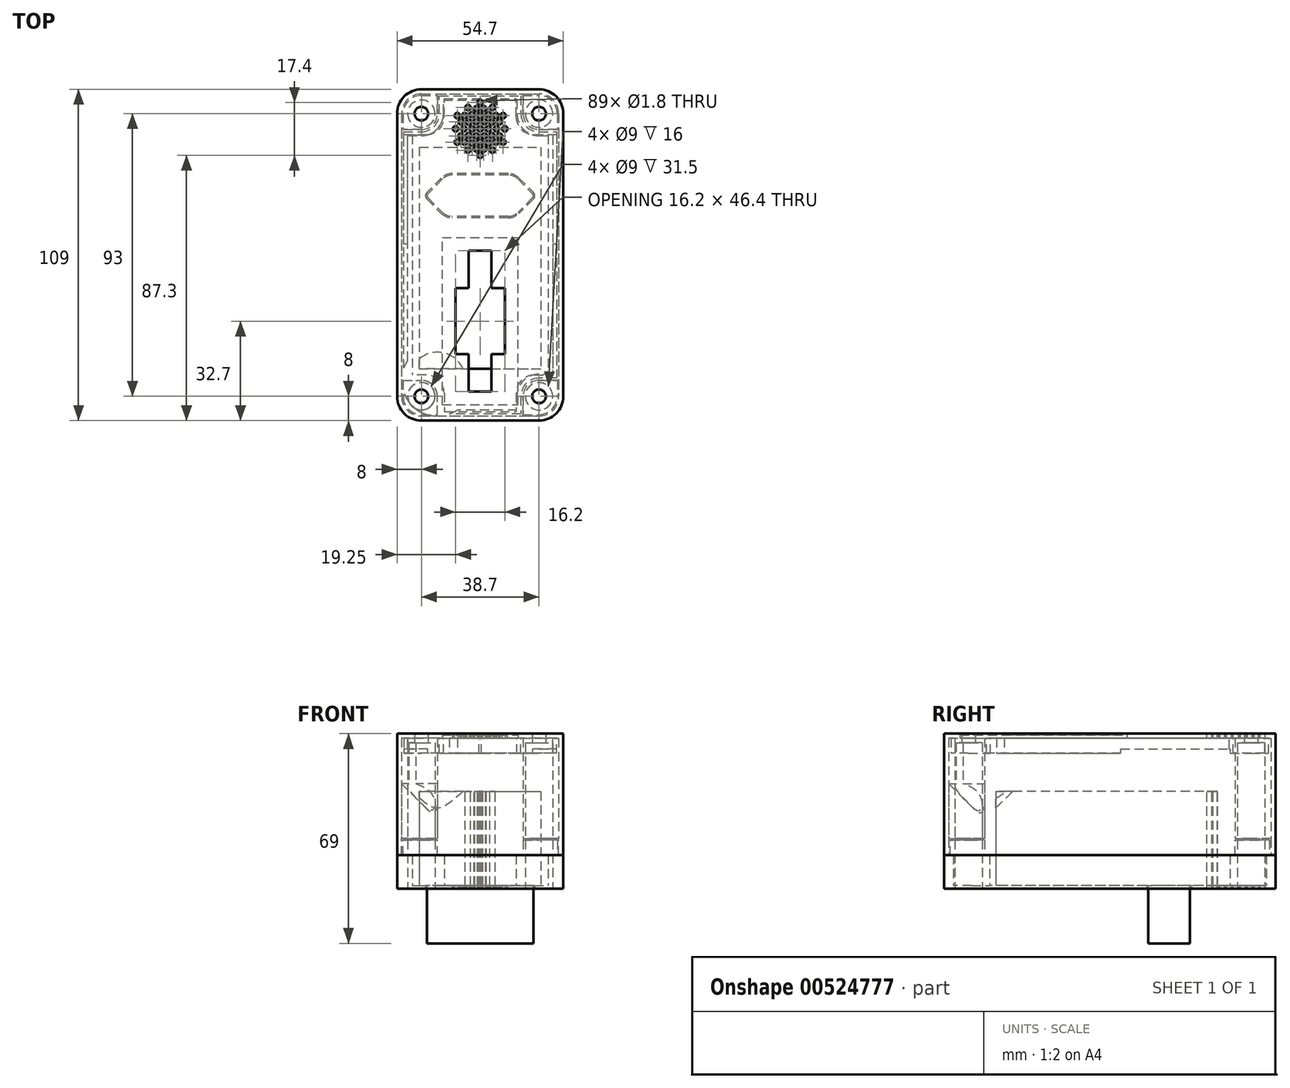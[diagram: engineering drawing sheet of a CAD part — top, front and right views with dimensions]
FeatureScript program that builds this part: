
annotation { "Feature Type Name" : "Feature", "Feature Type Description" : "" }
export const myFeature = defineFeature(function(context is Context, id is Id, definition is map)
    precondition{}
    {
        {
            var Q0;
            Q0=qCreatedBy(makeId("Top.planeOp"),FACE);
            var sketch = newSketch(context, id + "F0", { "sketchPlane" : qUnion([Q0])});
            skLineSegment(sketch, "E0.bottom", {"start": v(9.23, 7.3) * mm, "end": v(-9.23, 7.3) * mm});
            skLineSegment(sketch, "E0.top", {"start": v(9.23, -7.3) * mm, "end": v(-9.23, -7.3) * mm});
            skPoint(sketch, "E0.middle", {"position": v(0, 0) * mm});
            skLineSegment(sketch, "E1", {"start": v(12.76, 5.84) * mm, "end": v(17.54, 1.06) * mm});
            skLineSegment(sketch, "E2", {"start": v(17.54, -1.06) * mm, "end": v(12.76, -5.84) * mm});
            skLineSegment(sketch, "E3.MirrorCS", {"start": v(-12.76, 5.84) * mm, "end": v(-17.54, 1.06) * mm});
            skLineSegment(sketch, "E4.MirrorCS", {"start": v(-17.54, -1.06) * mm, "end": v(-12.76, -5.84) * mm});
            skPoint(sketch, "E5.visualSharp", {"position": v(-11.3, 7.3) * mm});
            skArc(sketch, "E5.filletArc", {"start": v(-9.23, 7.3) * mm, "mid": v(-11.14, 6.92) * mm, "end": v(-12.76, 5.84) * mm});
            skPoint(sketch, "E6.visualSharp", {"position": v(11.3, 7.3) * mm});
            skArc(sketch, "E6.filletArc", {"start": v(12.76, 5.84) * mm, "mid": v(11.14, 6.92) * mm, "end": v(9.23, 7.3) * mm});
            skPoint(sketch, "E7.visualSharp", {"position": v(11.3, -7.3) * mm});
            skArc(sketch, "E7.filletArc", {"start": v(9.23, -7.3) * mm, "mid": v(11.14, -6.92) * mm, "end": v(12.76, -5.84) * mm});
            skPoint(sketch, "E8.visualSharp", {"position": v(-11.3, -7.3) * mm});
            skArc(sketch, "E8.filletArc", {"start": v(-12.76, -5.84) * mm, "mid": v(-11.14, -6.92) * mm, "end": v(-9.23, -7.3) * mm});
            skPoint(sketch, "E9.visualSharp", {"position": v(-18.6, 0) * mm});
            skArc(sketch, "E9.filletArc", {"start": v(-17.54, 1.06) * mm, "mid": v(-17.98, 0) * mm, "end": v(-17.54, -1.06) * mm});
            skPoint(sketch, "E10.visualSharp", {"position": v(18.6, 0) * mm});
            skArc(sketch, "E10.filletArc", {"start": v(17.54, -1.06) * mm, "mid": v(17.98, 0) * mm, "end": v(17.54, 1.06) * mm});
            skLineSegment(sketch, "E11.bottom", {"start": v(-19.35, 35) * mm, "end": v(19.35, 35) * mm});
            skLineSegment(sketch, "E11.top", {"start": v(-19.35, -74) * mm, "end": v(19.35, -74) * mm});
            skLineSegment(sketch, "E11.left", {"start": v(-27.35, 27) * mm, "end": v(-27.35, -66) * mm});
            skLineSegment(sketch, "E11.right", {"start": v(27.35, 27) * mm, "end": v(27.35, -66) * mm});
            skPoint(sketch, "E12.visualSharp", {"position": v(27.35, 35) * mm});
            skArc(sketch, "E12.filletArc", {"start": v(27.35, 27) * mm, "mid": v(25, 32.66) * mm, "end": v(19.35, 35) * mm});
            skPoint(sketch, "E13.visualSharp", {"position": v(-27.35, 35) * mm});
            skArc(sketch, "E13.filletArc", {"start": v(-19.35, 35) * mm, "mid": v(-25, 32.66) * mm, "end": v(-27.35, 27) * mm});
            skPoint(sketch, "E14.visualSharp", {"position": v(-27.35, -74) * mm});
            skArc(sketch, "E14.filletArc", {"start": v(-27.35, -66) * mm, "mid": v(-25, -71.66) * mm, "end": v(-19.35, -74) * mm});
            skPoint(sketch, "E15.visualSharp", {"position": v(27.35, -74) * mm});
            skArc(sketch, "E15.filletArc", {"start": v(19.35, -74) * mm, "mid": v(25, -71.66) * mm, "end": v(27.35, -66) * mm});
            skLineSegment(sketch, "E16.bottom", {"start": v(-25.35, 25) * mm, "end": v(25.35, 25) * mm, "construction": true});
            skLineSegment(sketch, "E16.top", {"start": v(-25.35, -45) * mm, "end": v(25.35, -45) * mm, "construction": true});
            skLineSegment(sketch, "E16.left", {"start": v(-25.35, 25) * mm, "end": v(-25.35, -45) * mm, "construction": true});
            skLineSegment(sketch, "E16.right", {"start": v(25.35, 25) * mm, "end": v(25.35, -45) * mm, "construction": true});
            skSolve(sketch);
        }
        {
            var Q0;
            Q0=makeQuery(id+"F0.imprint","IMPRINT",FACE,{"disambiguationData":[TD([[makeQuery(id+"F0.imprint","IMPRINT",EDGE,{"derivedFrom":sQuery(id+"F0.wireOp",EDGE,"E0.bottom")}),-1.0]])]});
            extrude(context, id + "F1", {"entities" : qUnion([Q0]), "depth" : 1 * mm, "offsetDistance" : 25 * mm});
        }
        {
            var Q0;
            Q0=makeQuery(id+"F1.opExtrude","CAP_FACE",FACE,{"disambiguationData":[OSD([sQuery(id+"F0.wireOp",EDGE,"E0.bottom"),sQuery(id+"F0.wireOp",EDGE,"E0.top"),sQuery(id+"F0.wireOp",EDGE,"E1"),sQuery(id+"F0.wireOp",EDGE,"E2"),sQuery(id+"F0.wireOp",EDGE,"E3.MirrorCS"),sQuery(id+"F0.wireOp",EDGE,"E4.MirrorCS"),sQuery(id+"F0.wireOp",EDGE,"E5.filletArc"),sQuery(id+"F0.wireOp",EDGE,"E6.filletArc"),sQuery(id+"F0.wireOp",EDGE,"E7.filletArc"),sQuery(id+"F0.wireOp",EDGE,"E8.filletArc"),sQuery(id+"F0.wireOp",EDGE,"E9.filletArc"),sQuery(id+"F0.wireOp",EDGE,"E10.filletArc"),sQuery(id+"F0.wireOp",EDGE,"E11.bottom"),sQuery(id+"F0.wireOp",EDGE,"E11.top"),sQuery(id+"F0.wireOp",EDGE,"E11.left"),sQuery(id+"F0.wireOp",EDGE,"E11.right"),sQuery(id+"F0.wireOp",EDGE,"E12.filletArc"),sQuery(id+"F0.wireOp",EDGE,"E13.filletArc"),sQuery(id+"F0.wireOp",EDGE,"E14.filletArc"),sQuery(id+"F0.wireOp",EDGE,"E15.filletArc")])],"isStart":false});
            var sketch = newSketch(context, id + "F2", { "sketchPlane" : qUnion([Q0])});
            skLineSegment(sketch, "E17.bottom", {"start": v(-22.35, 20) * mm, "end": v(-17.85, 20) * mm});
            skLineSegment(sketch, "E17.top", {"start": v(17.85, -59) * mm, "end": v(22.35, -59) * mm});
            skLineSegment(sketch, "E17.left", {"start": v(-22.35, 20) * mm, "end": v(-22.35, -59) * mm});
            skLineSegment(sketch, "E17.right", {"start": v(22.35, 20) * mm, "end": v(22.35, -59) * mm});
            skCircle(sketch, "E18", {"center": v(19.35, 27) * mm, "radius": 4.5 * mm, "construction": true});
            skCircle(sketch, "E19", {"center": v(-19.35, 27) * mm, "radius": 4.5 * mm, "construction": true});
            skCircle(sketch, "E20", {"center": v(-19.35, -66) * mm, "radius": 4.5 * mm, "construction": true});
            skCircle(sketch, "E21", {"center": v(19.35, -66) * mm, "radius": 4.5 * mm, "construction": true});
            skCircle(sketch, "E22", {"center": v(-19.35, 27) * mm, "radius": 1.75 * mm, "construction": true});
            skCircle(sketch, "E23", {"center": v(19.35, 27) * mm, "radius": 1.75 * mm, "construction": true});
            skCircle(sketch, "E24", {"center": v(19.35, -66) * mm, "radius": 1.75 * mm, "construction": true});
            skCircle(sketch, "E25", {"center": v(-19.35, -66) * mm, "radius": 1.75 * mm, "construction": true});
            skLineSegment(sketch, "E26.top", {"start": v(-11.85, -71) * mm, "end": v(11.85, -71) * mm});
            skLineSegment(sketch, "E26.left", {"start": v(-11.85, -65) * mm, "end": v(-11.85, -71) * mm});
            skLineSegment(sketch, "E26.right", {"start": v(11.85, -65) * mm, "end": v(11.85, -71) * mm});
            skPoint(sketch, "E27.newPointA", {"position": v(11.85, -59) * mm});
            skArc(sketch, "E27.filletArc", {"start": v(17.85, -59) * mm, "mid": v(13.6, -60.76) * mm, "end": v(11.85, -65) * mm});
            skLineSegment(sketch, "E28", {"start": v(-17.85, -59) * mm, "end": v(-22.35, -59) * mm});
            skPoint(sketch, "E29.visualSharp", {"position": v(-11.85, -59) * mm});
            skArc(sketch, "E29.filletArc", {"start": v(-11.85, -65) * mm, "mid": v(-13.6, -60.76) * mm, "end": v(-17.85, -59) * mm});
            skLineSegment(sketch, "E30", {"start": v(27.35, -19.5) * mm, "end": v(-27.35, -19.5) * mm, "construction": true});
            skPoint(sketch, "E30.endSnap0", {"position": v(-27.35, -19.5) * mm});
            skArc(sketch, "E31.MirrorCS", {"start": v(-11.85, 26) * mm, "mid": v(-13.6, 21.76) * mm, "end": v(-17.85, 20) * mm});
            skLineSegment(sketch, "E32.MirrorCS", {"start": v(-11.85, 26) * mm, "end": v(-11.85, 32) * mm});
            skLineSegment(sketch, "E33.MirrorCS", {"start": v(-11.85, 32) * mm, "end": v(11.85, 32) * mm});
            skLineSegment(sketch, "E34.MirrorCS", {"start": v(11.85, 26) * mm, "end": v(11.85, 32) * mm});
            skArc(sketch, "E35.MirrorCS", {"start": v(17.85, 20) * mm, "mid": v(13.6, 21.76) * mm, "end": v(11.85, 26) * mm});
            skLineSegment(sketch, "E36.trimOffspring", {"start": v(17.85, 20) * mm, "end": v(22.35, 20) * mm});
            skSolve(sketch);
        }
        {
            var Q0;
            Q0=makeQuery(id+"F2.imprint","IMPRINT",FACE,{"disambiguationData":[TD([[makeQuery(id+"F2.imprint","IMPRINT",EDGE,{"derivedFrom":sQuery(id+"F2.wireOp",EDGE,"E17.bottom")}),1.0]])]});
            extrude(context, id + "F3", {"entities" : qUnion([Q0]), "operationType" : NewBodyOperationType.ADD, "depth" : 15 * mm, "offsetDistance" : 25 * mm});
        }
        {
            var Q0;
            Q0=makeQuery(id+"F1.opExtrude","CAP_FACE",FACE,{"disambiguationData":[OSD([sQuery(id+"F0.wireOp",EDGE,"E0.bottom"),sQuery(id+"F0.wireOp",EDGE,"E0.top"),sQuery(id+"F0.wireOp",EDGE,"E1"),sQuery(id+"F0.wireOp",EDGE,"E2"),sQuery(id+"F0.wireOp",EDGE,"E3.MirrorCS"),sQuery(id+"F0.wireOp",EDGE,"E4.MirrorCS"),sQuery(id+"F0.wireOp",EDGE,"E5.filletArc"),sQuery(id+"F0.wireOp",EDGE,"E6.filletArc"),sQuery(id+"F0.wireOp",EDGE,"E7.filletArc"),sQuery(id+"F0.wireOp",EDGE,"E8.filletArc"),sQuery(id+"F0.wireOp",EDGE,"E9.filletArc"),sQuery(id+"F0.wireOp",EDGE,"E10.filletArc"),sQuery(id+"F0.wireOp",EDGE,"E11.bottom"),sQuery(id+"F0.wireOp",EDGE,"E11.top"),sQuery(id+"F0.wireOp",EDGE,"E11.left"),sQuery(id+"F0.wireOp",EDGE,"E11.right"),sQuery(id+"F0.wireOp",EDGE,"E12.filletArc"),sQuery(id+"F0.wireOp",EDGE,"E13.filletArc"),sQuery(id+"F0.wireOp",EDGE,"E14.filletArc"),sQuery(id+"F0.wireOp",EDGE,"E15.filletArc")])],"isStart":true});
            var sketch = newSketch(context, id + "F4", { "sketchPlane" : qUnion([Q0])});
            skCircle(sketch, "E37.0", {"center": v(-19.35, 66) * mm, "radius": 1.75 * mm});
            skCircle(sketch, "E38.0", {"center": v(-19.35, 66) * mm, "radius": 4.5 * mm});
            skCircle(sketch, "E39.0", {"center": v(19.35, 66) * mm, "radius": 1.75 * mm});
            skCircle(sketch, "E40.0", {"center": v(19.35, 66) * mm, "radius": 4.5 * mm});
            skCircle(sketch, "E41.0", {"center": v(19.35, -27) * mm, "radius": 1.75 * mm});
            skCircle(sketch, "E42.0", {"center": v(19.35, -27) * mm, "radius": 4.5 * mm});
            skCircle(sketch, "E43.0", {"center": v(-19.35, -27) * mm, "radius": 1.75 * mm});
            skCircle(sketch, "E44.0", {"center": v(-19.35, -27) * mm, "radius": 4.5 * mm});
            skSolve(sketch);
        }
        {
            var Q0;
            Q0=makeQuery(id+"F4.imprint","IMPRINT",FACE,{"disambiguationData":[TD([[makeQuery(id+"F4.imprint","IMPRINT",EDGE,{"derivedFrom":sQuery(id+"F4.wireOp",EDGE,"E37.0")}),1.0]])]});
            var Q1;
            Q1=makeQuery(id+"F4.imprint","IMPRINT",FACE,{"disambiguationData":[TD([[makeQuery(id+"F4.imprint","IMPRINT",EDGE,{"derivedFrom":sQuery(id+"F4.wireOp",EDGE,"E39.0")}),1.0]])]});
            var Q2;
            Q2=makeQuery(id+"F4.imprint","IMPRINT",FACE,{"disambiguationData":[TD([[makeQuery(id+"F4.imprint","IMPRINT",EDGE,{"derivedFrom":sQuery(id+"F4.wireOp",EDGE,"E43.0")}),1.0]])]});
            var Q3;
            Q3=makeQuery(id+"F4.imprint","IMPRINT",FACE,{"disambiguationData":[TD([[makeQuery(id+"F4.imprint","IMPRINT",EDGE,{"derivedFrom":sQuery(id+"F4.wireOp",EDGE,"E41.0")}),1.0]])]});
            extrude(context, id + "F5", {"entities" : qUnion([Q0, Q1, Q2, Q3]), "operationType" : NewBodyOperationType.REMOVE, "oppositeDirection" : true, "depth" : 5.5 * mm, "offsetDistance" : 25 * mm});
        }
        {
            var Q0;
            Q0=makeQuery(id+"F3.opExtrude","CAP_FACE",FACE,{"disambiguationData":[OSD([sQuery(id+"F0.wireOp",EDGE,"E11.bottom"),sQuery(id+"F0.wireOp",EDGE,"E11.top"),sQuery(id+"F0.wireOp",EDGE,"E11.left"),sQuery(id+"F0.wireOp",EDGE,"E11.right"),sQuery(id+"F0.wireOp",EDGE,"E12.filletArc"),sQuery(id+"F0.wireOp",EDGE,"E13.filletArc"),sQuery(id+"F0.wireOp",EDGE,"E14.filletArc"),sQuery(id+"F0.wireOp",EDGE,"E15.filletArc"),sQuery(id+"F2.wireOp",EDGE,"E17.bottom"),sQuery(id+"F2.wireOp",EDGE,"E17.top"),sQuery(id+"F2.wireOp",EDGE,"E17.left"),sQuery(id+"F2.wireOp",EDGE,"E17.right"),sQuery(id+"F2.wireOp",EDGE,"E26.top"),sQuery(id+"F2.wireOp",EDGE,"E26.left"),sQuery(id+"F2.wireOp",EDGE,"E26.right"),sQuery(id+"F2.wireOp",EDGE,"E27.filletArc"),sQuery(id+"F2.wireOp",EDGE,"E28"),sQuery(id+"F2.wireOp",EDGE,"E29.filletArc"),sQuery(id+"F2.wireOp",EDGE,"E31.MirrorCS"),sQuery(id+"F2.wireOp",EDGE,"E32.MirrorCS"),sQuery(id+"F2.wireOp",EDGE,"E33.MirrorCS"),sQuery(id+"F2.wireOp",EDGE,"E34.MirrorCS"),sQuery(id+"F2.wireOp",EDGE,"E35.MirrorCS"),sQuery(id+"F2.wireOp",EDGE,"E36.trimOffspring")])],"isStart":false});
            var sketch = newSketch(context, id + "F6", { "sketchPlane" : qUnion([Q0])});
            skLineSegment(sketch, "E45.0", {"start": v(-19.35, 33) * mm, "end": v(19.35, 33) * mm});
            skArc(sketch, "E45.1", {"start": v(25.35, 27) * mm, "mid": v(23.6, 31.24) * mm, "end": v(19.35, 33) * mm});
            skArc(sketch, "E45.2", {"start": v(-19.35, 33) * mm, "mid": v(-23.6, 31.24) * mm, "end": v(-25.35, 27) * mm});
            skLineSegment(sketch, "E45.3", {"start": v(25.35, 27) * mm, "end": v(25.35, -66) * mm});
            skLineSegment(sketch, "E45.4", {"start": v(-25.35, 27) * mm, "end": v(-25.35, -66) * mm});
            skArc(sketch, "E45.5", {"start": v(-25.35, -66) * mm, "mid": v(-23.6, -70.24) * mm, "end": v(-19.35, -72) * mm});
            skLineSegment(sketch, "E45.6", {"start": v(-19.35, -72) * mm, "end": v(19.35, -72) * mm});
            skArc(sketch, "E45.7", {"start": v(19.35, -72) * mm, "mid": v(23.6, -70.24) * mm, "end": v(25.35, -66) * mm});
            skArc(sketch, "E46.0", {"start": v(-19.35, 35) * mm, "mid": v(-25, 32.66) * mm, "end": v(-27.35, 27) * mm});
            skLineSegment(sketch, "E47.0", {"start": v(-19.35, 35) * mm, "end": v(19.35, 35) * mm});
            skArc(sketch, "E48.0", {"start": v(27.35, 27) * mm, "mid": v(25, 32.66) * mm, "end": v(19.35, 35) * mm});
            skLineSegment(sketch, "E49.0", {"start": v(27.35, 27) * mm, "end": v(27.35, -66) * mm});
            skArc(sketch, "E50.0", {"start": v(19.35, -74) * mm, "mid": v(25, -71.66) * mm, "end": v(27.35, -66) * mm});
            skLineSegment(sketch, "E51.0", {"start": v(-19.35, -74) * mm, "end": v(19.35, -74) * mm});
            skArc(sketch, "E52.0", {"start": v(-27.35, -66) * mm, "mid": v(-25, -71.66) * mm, "end": v(-19.35, -74) * mm});
            skLineSegment(sketch, "E53.0", {"start": v(-27.35, 27) * mm, "end": v(-27.35, -66) * mm});
            skSolve(sketch);
        }
        {
            var Q0;
            Q0 = qSketchRegion(id + "F6", true);
            extrude(context, id + "F7", {"entities" : qUnion([Q0]), "operationType" : NewBodyOperationType.REMOVE, "oppositeDirection" : true, "depth" : 5 * mm, "offsetDistance" : 25 * mm});
        }
        {
            var Q0;
            Q0=makeQuery(id+"F1.opExtrude","CAP_FACE",FACE,{"disambiguationData":[OSD([sQuery(id+"F0.wireOp",EDGE,"E0.bottom"),sQuery(id+"F0.wireOp",EDGE,"E0.top"),sQuery(id+"F0.wireOp",EDGE,"E1"),sQuery(id+"F0.wireOp",EDGE,"E2"),sQuery(id+"F0.wireOp",EDGE,"E3.MirrorCS"),sQuery(id+"F0.wireOp",EDGE,"E4.MirrorCS"),sQuery(id+"F0.wireOp",EDGE,"E5.filletArc"),sQuery(id+"F0.wireOp",EDGE,"E6.filletArc"),sQuery(id+"F0.wireOp",EDGE,"E7.filletArc"),sQuery(id+"F0.wireOp",EDGE,"E8.filletArc"),sQuery(id+"F0.wireOp",EDGE,"E9.filletArc"),sQuery(id+"F0.wireOp",EDGE,"E10.filletArc"),sQuery(id+"F0.wireOp",EDGE,"E11.bottom"),sQuery(id+"F0.wireOp",EDGE,"E11.top"),sQuery(id+"F0.wireOp",EDGE,"E11.left"),sQuery(id+"F0.wireOp",EDGE,"E11.right"),sQuery(id+"F0.wireOp",EDGE,"E12.filletArc"),sQuery(id+"F0.wireOp",EDGE,"E13.filletArc"),sQuery(id+"F0.wireOp",EDGE,"E14.filletArc"),sQuery(id+"F0.wireOp",EDGE,"E15.filletArc")])],"isStart":false});
            cPlane(context, id + "F8", {"entities" : qUnion([Q0]), "cplaneType" : CPlaneType.OFFSET, "offset" : 50 * mm, "width" : 150 * mm, "height" : 150 * mm});
        }
        {
            var Q0;
            Q0=qCreatedBy(id+"F8.planeOp",FACE);
            var sketch = newSketch(context, id + "F9", { "sketchPlane" : qUnion([Q0])});
            skLineSegment(sketch, "E54.0", {"start": v(-19.35, 35) * mm, "end": v(19.35, 35) * mm});
            skArc(sketch, "E55.0", {"start": v(-19.35, 35) * mm, "mid": v(-25, 32.66) * mm, "end": v(-27.35, 27) * mm});
            skLineSegment(sketch, "E56.0", {"start": v(-27.35, 27) * mm, "end": v(-27.35, -66) * mm});
            skArc(sketch, "E57.0", {"start": v(-27.35, -66) * mm, "mid": v(-25, -71.66) * mm, "end": v(-19.35, -74) * mm});
            skLineSegment(sketch, "E58.0", {"start": v(-19.35, -74) * mm, "end": v(19.35, -74) * mm});
            skArc(sketch, "E59.0", {"start": v(19.35, -74) * mm, "mid": v(25, -71.66) * mm, "end": v(27.35, -66) * mm});
            skLineSegment(sketch, "E60.0", {"start": v(27.35, 27) * mm, "end": v(27.35, -66) * mm});
            skArc(sketch, "E61.0", {"start": v(27.35, 27) * mm, "mid": v(25, 32.66) * mm, "end": v(19.35, 35) * mm});
            skSolve(sketch);
        }
        {
            var Q0;
            Q0=makeQuery(id+"F9.imprint","IMPRINT",FACE,{"disambiguationData":[TD([[makeQuery(id+"F9.imprint","IMPRINT",EDGE,{"derivedFrom":sQuery(id+"F9.wireOp",EDGE,"E54.0")}),-1.0]])]});
            var Q1;
            Q1=makeQuery(id+"F7.boolean.opBoolean","COPY",FACE,{"derivedFrom":makeQuery(id+"F7.opExtrude","CAP_FACE",FACE,{"disambiguationData":[OSD([sQuery(id+"F6.wireOp",EDGE,"E45.0"),sQuery(id+"F6.wireOp",EDGE,"E45.1"),sQuery(id+"F6.wireOp",EDGE,"E45.2"),sQuery(id+"F6.wireOp",EDGE,"E45.3"),sQuery(id+"F6.wireOp",EDGE,"E45.4"),sQuery(id+"F6.wireOp",EDGE,"E45.5"),sQuery(id+"F6.wireOp",EDGE,"E45.6"),sQuery(id+"F6.wireOp",EDGE,"E45.7"),sQuery(id+"F6.wireOp",EDGE,"E46.0"),sQuery(id+"F6.wireOp",EDGE,"E47.0"),sQuery(id+"F6.wireOp",EDGE,"E48.0"),sQuery(id+"F6.wireOp",EDGE,"E49.0"),sQuery(id+"F6.wireOp",EDGE,"E50.0"),sQuery(id+"F6.wireOp",EDGE,"E51.0"),sQuery(id+"F6.wireOp",EDGE,"E52.0"),sQuery(id+"F6.wireOp",EDGE,"E53.0")])],"isStart":false})});
            extrude(context, id + "F10", {"entities" : qUnion([Q0]), "endBound" : BoundingType.UP_TO_SURFACE, "oppositeDirection" : true, "depth" : 25 * mm, "endBoundEntityFace" : qUnion([Q1]), "offsetDistance" : 25 * mm});
        }
        {
            var Q0;
            Q0=makeQuery(id+"F1.opExtrude","SWEPT_BODY",BODY,{"disambiguationData":[OSD([sQuery(id+"F0.wireOp",EDGE,"E0.bottom"),sQuery(id+"F0.wireOp",EDGE,"E0.top"),sQuery(id+"F0.wireOp",EDGE,"E1"),sQuery(id+"F0.wireOp",EDGE,"E2"),sQuery(id+"F0.wireOp",EDGE,"E3.MirrorCS"),sQuery(id+"F0.wireOp",EDGE,"E4.MirrorCS"),sQuery(id+"F0.wireOp",EDGE,"E5.filletArc"),sQuery(id+"F0.wireOp",EDGE,"E6.filletArc"),sQuery(id+"F0.wireOp",EDGE,"E7.filletArc"),sQuery(id+"F0.wireOp",EDGE,"E8.filletArc"),sQuery(id+"F0.wireOp",EDGE,"E9.filletArc"),sQuery(id+"F0.wireOp",EDGE,"E10.filletArc"),sQuery(id+"F0.wireOp",EDGE,"E11.bottom"),sQuery(id+"F0.wireOp",EDGE,"E11.top"),sQuery(id+"F0.wireOp",EDGE,"E11.left"),sQuery(id+"F0.wireOp",EDGE,"E11.right"),sQuery(id+"F0.wireOp",EDGE,"E12.filletArc"),sQuery(id+"F0.wireOp",EDGE,"E13.filletArc"),sQuery(id+"F0.wireOp",EDGE,"E14.filletArc"),sQuery(id+"F0.wireOp",EDGE,"E15.filletArc")])]});
            var Q1;
            Q1=makeQuery(id+"F10.opExtrude","SWEPT_BODY",BODY,{"disambiguationData":[OSD([sQuery(id+"F9.wireOp",EDGE,"E54.0"),sQuery(id+"F9.wireOp",EDGE,"E55.0"),sQuery(id+"F9.wireOp",EDGE,"E56.0"),sQuery(id+"F9.wireOp",EDGE,"E57.0"),sQuery(id+"F9.wireOp",EDGE,"E58.0"),sQuery(id+"F9.wireOp",EDGE,"E59.0"),sQuery(id+"F9.wireOp",EDGE,"E60.0"),sQuery(id+"F9.wireOp",EDGE,"E61.0")])]});
            var Q2;
            Q2=makeQuery(id+"F3.opExtrude","CAP_FACE",FACE,{"disambiguationData":[OSD([sQuery(id+"F0.wireOp",EDGE,"E11.bottom"),sQuery(id+"F0.wireOp",EDGE,"E11.top"),sQuery(id+"F0.wireOp",EDGE,"E11.left"),sQuery(id+"F0.wireOp",EDGE,"E11.right"),sQuery(id+"F0.wireOp",EDGE,"E12.filletArc"),sQuery(id+"F0.wireOp",EDGE,"E13.filletArc"),sQuery(id+"F0.wireOp",EDGE,"E14.filletArc"),sQuery(id+"F0.wireOp",EDGE,"E15.filletArc"),sQuery(id+"F2.wireOp",EDGE,"E17.bottom"),sQuery(id+"F2.wireOp",EDGE,"E17.top"),sQuery(id+"F2.wireOp",EDGE,"E17.left"),sQuery(id+"F2.wireOp",EDGE,"E17.right"),sQuery(id+"F2.wireOp",EDGE,"E26.top"),sQuery(id+"F2.wireOp",EDGE,"E26.left"),sQuery(id+"F2.wireOp",EDGE,"E26.right"),sQuery(id+"F2.wireOp",EDGE,"E27.filletArc"),sQuery(id+"F2.wireOp",EDGE,"E28"),sQuery(id+"F2.wireOp",EDGE,"E29.filletArc"),sQuery(id+"F2.wireOp",EDGE,"E31.MirrorCS"),sQuery(id+"F2.wireOp",EDGE,"E32.MirrorCS"),sQuery(id+"F2.wireOp",EDGE,"E33.MirrorCS"),sQuery(id+"F2.wireOp",EDGE,"E34.MirrorCS"),sQuery(id+"F2.wireOp",EDGE,"E35.MirrorCS"),sQuery(id+"F2.wireOp",EDGE,"E36.trimOffspring")])],"isStart":false});
            var Q3;
            Q3=makeQuery(id+"F7.boolean.opBoolean","COPY",FACE,{"derivedFrom":makeQuery(id+"F7.opExtrude","SWEPT_FACE",FACE,{"disambiguationData":[OSD([sQuery(id+"F6.wireOp",EDGE,"E45.3")])]})});
            var Q4;
            Q4=makeQuery(id+"F7.boolean.opBoolean","COPY",FACE,{"derivedFrom":makeQuery(id+"F7.opExtrude","SWEPT_FACE",FACE,{"disambiguationData":[OSD([sQuery(id+"F6.wireOp",EDGE,"E45.1")])]})});
            var Q5;
            Q5=makeQuery(id+"F7.boolean.opBoolean","COPY",FACE,{"derivedFrom":makeQuery(id+"F7.opExtrude","SWEPT_FACE",FACE,{"disambiguationData":[OSD([sQuery(id+"F6.wireOp",EDGE,"E45.2")])]})});
            var Q6;
            Q6=makeQuery(id+"F7.boolean.opBoolean","COPY",FACE,{"derivedFrom":makeQuery(id+"F7.opExtrude","SWEPT_FACE",FACE,{"disambiguationData":[OSD([sQuery(id+"F6.wireOp",EDGE,"E45.0")])]})});
            var Q7;
            Q7=makeQuery(id+"F7.boolean.opBoolean","COPY",FACE,{"derivedFrom":makeQuery(id+"F7.opExtrude","SWEPT_FACE",FACE,{"disambiguationData":[OSD([sQuery(id+"F6.wireOp",EDGE,"E45.4")])]})});
            var Q8;
            Q8=makeQuery(id+"F7.boolean.opBoolean","COPY",FACE,{"derivedFrom":makeQuery(id+"F7.opExtrude","SWEPT_FACE",FACE,{"disambiguationData":[OSD([sQuery(id+"F6.wireOp",EDGE,"E45.5")])]})});
            var Q9;
            Q9=makeQuery(id+"F7.boolean.opBoolean","COPY",FACE,{"derivedFrom":makeQuery(id+"F7.opExtrude","SWEPT_FACE",FACE,{"disambiguationData":[OSD([sQuery(id+"F6.wireOp",EDGE,"E45.6")])]})});
            var Q10;
            Q10=makeQuery(id+"F7.boolean.opBoolean","COPY",FACE,{"derivedFrom":makeQuery(id+"F7.opExtrude","SWEPT_FACE",FACE,{"disambiguationData":[OSD([sQuery(id+"F6.wireOp",EDGE,"E45.7")])]})});
            booleanBodies(context, id + "F11", {"operationType" : BooleanOperationType.SUBTRACTION, "tools" : qUnion([Q0]), "targets" : qUnion([Q1]), "offset" : true, "entitiesToOffset" : qUnion([Q2, Q3, Q4, Q5, Q6, Q7, Q8, Q9, Q10]), "offsetDistance" : .5 * mm, "keepTools" : true});
        }
        {
            var Q0;
            Q0=makeQuery(id+"F4.imprint","IMPRINT",FACE,{"disambiguationData":[TD([[makeQuery(id+"F4.imprint","IMPRINT",EDGE,{"derivedFrom":sQuery(id+"F4.wireOp",EDGE,"E37.0")}),-1.0]])]});
            var Q1;
            Q1=makeQuery(id+"F4.imprint","IMPRINT",FACE,{"disambiguationData":[TD([[makeQuery(id+"F4.imprint","IMPRINT",EDGE,{"derivedFrom":sQuery(id+"F4.wireOp",EDGE,"E39.0")}),-1.0]])]});
            var Q2;
            Q2=makeQuery(id+"F4.imprint","IMPRINT",FACE,{"disambiguationData":[TD([[makeQuery(id+"F4.imprint","IMPRINT",EDGE,{"derivedFrom":sQuery(id+"F4.wireOp",EDGE,"E41.0")}),-1.0]])]});
            var Q3;
            Q3=makeQuery(id+"F4.imprint","IMPRINT",FACE,{"disambiguationData":[TD([[makeQuery(id+"F4.imprint","IMPRINT",EDGE,{"derivedFrom":sQuery(id+"F4.wireOp",EDGE,"E43.0")}),-1.0]])]});
            extrude(context, id + "F12", {"entities" : qUnion([Q0, Q1, Q2, Q3]), "operationType" : NewBodyOperationType.REMOVE, "oppositeDirection" : true, "depth" : 48 * mm, "offsetDistance" : 25 * mm});
        }
        {
            var Q0;
            Q0=makeQuery(id+"F11.tempBoolean.opBoolean","SPLIT",FACE,{"disambiguationData":[TD([makeQuery(id+"F11.offsetTempBody.opPattern","COPY",FACE,{"derivedFrom":makeQuery(id+"F3.opExtrude","SWEPT_FACE",FACE,{"disambiguationData":[OSD([sQuery(id+"F2.wireOp",EDGE,"E17.bottom")])]}),"instanceName":"1"})])],"derivedFrom":makeQuery(id+"F10.opExtrude","CAP_FACE",FACE,{"disambiguationData":[OSD([sQuery(id+"F9.wireOp",EDGE,"E54.0"),sQuery(id+"F9.wireOp",EDGE,"E55.0"),sQuery(id+"F9.wireOp",EDGE,"E56.0"),sQuery(id+"F9.wireOp",EDGE,"E57.0"),sQuery(id+"F9.wireOp",EDGE,"E58.0"),sQuery(id+"F9.wireOp",EDGE,"E59.0"),sQuery(id+"F9.wireOp",EDGE,"E60.0"),sQuery(id+"F9.wireOp",EDGE,"E61.0")])],"isStart":false})});
            var sketch = newSketch(context, id + "F13", { "sketchPlane" : qUnion([Q0])});
            skLineSegment(sketch, "E62.0", {"start": v(-19.35, 72.5) * mm, "end": v(-14.1, 72.5) * mm, "construction": true});
            skArc(sketch, "E63.0", {"start": v(19.35, 72.5) * mm, "mid": v(23.95, 70.6) * mm, "end": v(25.85, 66) * mm, "construction": true});
            skLineSegment(sketch, "E64.0", {"start": v(25.85, -27) * mm, "end": v(25.85, -21.75) * mm, "construction": true});
            skArc(sketch, "E65.0", {"start": v(25.85, -27) * mm, "mid": v(23.95, -31.6) * mm, "end": v(19.35, -33.5) * mm, "construction": true});
            skLineSegment(sketch, "E66.0", {"start": v(-19.35, -33.5) * mm, "end": v(-14.1, -33.5) * mm, "construction": true});
            skArc(sketch, "E67.0", {"start": v(-19.35, -33.5) * mm, "mid": v(-23.95, -31.6) * mm, "end": v(-25.85, -27) * mm, "construction": true});
            skLineSegment(sketch, "E68.0", {"start": v(-25.85, -27) * mm, "end": v(-25.85, -21.75) * mm, "construction": true});
            skArc(sketch, "E69.0", {"start": v(-25.85, 66) * mm, "mid": v(-23.95, 70.6) * mm, "end": v(-19.35, 72.5) * mm, "construction": true});
            skArc(sketch, "E70", {"start": v(-19.35, 60.75) * mm, "mid": v(-15.64, 62.29) * mm, "end": v(-14.1, 66) * mm});
            skLineSegment(sketch, "E71", {"start": v(-14.1, 66) * mm, "end": v(-14.1, 72.5) * mm});
            skLineSegment(sketch, "E72", {"start": v(-19.35, 60.75) * mm, "end": v(-25.85, 60.75) * mm});
            skLineSegment(sketch, "E73", {"start": v(-14.1, 72.5) * mm, "end": v(14.1, 72.5) * mm});
            skLineSegment(sketch, "E74", {"start": v(-25.85, 60.75) * mm, "end": v(-25.85, 66) * mm, "construction": true});
            skLineSegment(sketch, "E75", {"start": v(-25.85, 19.5) * mm, "end": v(25.85, 19.5) * mm, "construction": true});
            skLineSegment(sketch, "E76.MirrorCS", {"start": v(14.1, 66) * mm, "end": v(14.1, 72.5) * mm});
            skArc(sketch, "E77.MirrorCS", {"start": v(19.35, 60.75) * mm, "mid": v(15.64, 62.29) * mm, "end": v(14.1, 66) * mm});
            skLineSegment(sketch, "E78.MirrorCS", {"start": v(19.35, 60.75) * mm, "end": v(25.85, 60.75) * mm});
            skLineSegment(sketch, "E79.MirrorCS", {"start": v(-19.35, -21.75) * mm, "end": v(-25.85, -21.75) * mm});
            skArc(sketch, "E80.MirrorCS", {"start": v(-19.35, -21.75) * mm, "mid": v(-15.64, -23.29) * mm, "end": v(-14.1, -27) * mm});
            skLineSegment(sketch, "E81.MirrorCS", {"start": v(-14.1, -27) * mm, "end": v(-14.1, -33.5) * mm});
            skLineSegment(sketch, "E82.MirrorCS", {"start": v(14.1, -27) * mm, "end": v(14.1, -33.5) * mm});
            skArc(sketch, "E83.MirrorCS", {"start": v(19.35, -21.75) * mm, "mid": v(15.64, -23.29) * mm, "end": v(14.1, -27) * mm});
            skLineSegment(sketch, "E84.MirrorCS", {"start": v(19.35, -21.75) * mm, "end": v(25.85, -21.75) * mm});
            skLineSegment(sketch, "E85", {"start": v(14.1, 72.5) * mm, "end": v(19.35, 72.5) * mm, "construction": true});
            skLineSegment(sketch, "E86", {"start": v(25.85, 60.75) * mm, "end": v(25.85, 60.75) * mm});
            skLineSegment(sketch, "E87", {"start": v(25.85, -21.75) * mm, "end": v(25.85, -21.75) * mm});
            skLineSegment(sketch, "E88", {"start": v(14.1, -33.5) * mm, "end": v(19.35, -33.5) * mm, "construction": true});
            skLineSegment(sketch, "E89", {"start": v(-14.1, -33.5) * mm, "end": v(14.1, -33.5) * mm});
            skLineSegment(sketch, "E90", {"start": v(-25.85, -21.75) * mm, "end": v(-25.85, 60.75) * mm});
            skLineSegment(sketch, "E91", {"start": v(25.85, 60.75) * mm, "end": v(25.85, 66) * mm, "construction": true});
            skLineSegment(sketch, "E92", {"start": v(25.85, -21.75) * mm, "end": v(25.85, 60.75) * mm});
            skSolve(sketch);
        }
        {
            var Q0;
            Q0 = qSketchRegion(id + "F13", true);
            extrude(context, id + "F14", {"entities" : qUnion([Q0]), "operationType" : NewBodyOperationType.REMOVE, "oppositeDirection" : true, "depth" : 38.5 * mm, "offsetDistance" : 25 * mm});
        }
        {
            var Q0;
            Q0=makeQuery(id+"F14.boolean.opBoolean","COPY",FACE,{"derivedFrom":makeQuery(id+"F14.opExtrude","CAP_FACE",FACE,{"disambiguationData":[OSD([sQuery(id+"F13.wireOp",EDGE,"E70"),sQuery(id+"F13.wireOp",EDGE,"E71"),sQuery(id+"F13.wireOp",EDGE,"E72"),sQuery(id+"F13.wireOp",EDGE,"E73"),sQuery(id+"F13.wireOp",EDGE,"E76.MirrorCS"),sQuery(id+"F13.wireOp",EDGE,"E77.MirrorCS"),sQuery(id+"F13.wireOp",EDGE,"E78.MirrorCS"),sQuery(id+"F13.wireOp",EDGE,"E79.MirrorCS"),sQuery(id+"F13.wireOp",EDGE,"E80.MirrorCS"),sQuery(id+"F13.wireOp",EDGE,"E81.MirrorCS"),sQuery(id+"F13.wireOp",EDGE,"E82.MirrorCS"),sQuery(id+"F13.wireOp",EDGE,"E83.MirrorCS"),sQuery(id+"F13.wireOp",EDGE,"E84.MirrorCS"),sQuery(id+"F13.wireOp",EDGE,"E89"),sQuery(id+"F13.wireOp",EDGE,"E90"),sQuery(id+"F13.wireOp",EDGE,"E92")])],"isStart":false})});
            var sketch = newSketch(context, id + "F15", { "sketchPlane" : qUnion([Q0])});
            skLineSegment(sketch, "E93.0", {"start": v(13.4, -32.8) * mm, "end": v(13.4, -27) * mm});
            skLineSegment(sketch, "E93.1", {"start": v(-13.4, -32.8) * mm, "end": v(13.4, -32.8) * mm});
            skLineSegment(sketch, "E93.2", {"start": v(-13.4, -27) * mm, "end": v(-13.4, -32.8) * mm});
            skArc(sketch, "E93.3", {"start": v(-19.35, -21.05) * mm, "mid": v(-15.14, -22.8) * mm, "end": v(-13.4, -27) * mm});
            skLineSegment(sketch, "E93.4", {"start": v(-25.15, -21.05) * mm, "end": v(-19.35, -21.05) * mm});
            skArc(sketch, "E93.5", {"start": v(19.35, 60.05) * mm, "mid": v(15.14, 61.8) * mm, "end": v(13.4, 66) * mm});
            skLineSegment(sketch, "E93.6", {"start": v(25.15, 60.05) * mm, "end": v(19.35, 60.05) * mm});
            skLineSegment(sketch, "E93.7", {"start": v(25.15, -21.05) * mm, "end": v(25.15, 60.05) * mm});
            skLineSegment(sketch, "E93.8", {"start": v(19.35, -21.05) * mm, "end": v(25.15, -21.05) * mm});
            skLineSegment(sketch, "E93.9", {"start": v(13.4, 66) * mm, "end": v(13.4, 71.8) * mm});
            skLineSegment(sketch, "E93.10", {"start": v(13.4, 71.8) * mm, "end": v(-13.4, 71.8) * mm});
            skLineSegment(sketch, "E93.11", {"start": v(-13.4, 71.8) * mm, "end": v(-13.4, 66) * mm});
            skArc(sketch, "E93.12", {"start": v(-13.4, 66) * mm, "mid": v(-15.14, 61.8) * mm, "end": v(-19.35, 60.05) * mm});
            skLineSegment(sketch, "E93.13", {"start": v(-19.35, 60.05) * mm, "end": v(-25.15, 60.05) * mm});
            skArc(sketch, "E93.14", {"start": v(13.4, -27) * mm, "mid": v(15.14, -22.8) * mm, "end": v(19.35, -21.05) * mm});
            skLineSegment(sketch, "E93.15", {"start": v(-25.15, 60.05) * mm, "end": v(-25.15, -21.05) * mm});
            skLineSegment(sketch, "E94.0", {"start": v(12.1, -31.5) * mm, "end": v(12.1, -27) * mm});
            skLineSegment(sketch, "E94.1", {"start": v(-12.1, -31.5) * mm, "end": v(12.1, -31.5) * mm});
            skLineSegment(sketch, "E94.2", {"start": v(-12.1, -27) * mm, "end": v(-12.1, -31.5) * mm});
            skArc(sketch, "E94.3", {"start": v(-19.35, -19.75) * mm, "mid": v(-14.22, -21.87) * mm, "end": v(-12.1, -27) * mm});
            skLineSegment(sketch, "E94.4", {"start": v(-23.85, -19.75) * mm, "end": v(-19.35, -19.75) * mm});
            skArc(sketch, "E94.5", {"start": v(19.35, 58.75) * mm, "mid": v(14.22, 60.87) * mm, "end": v(12.1, 66) * mm});
            skLineSegment(sketch, "E94.6", {"start": v(23.85, 58.75) * mm, "end": v(19.35, 58.75) * mm});
            skLineSegment(sketch, "E94.7", {"start": v(23.85, -19.75) * mm, "end": v(23.85, 58.75) * mm});
            skLineSegment(sketch, "E94.8", {"start": v(19.35, -19.75) * mm, "end": v(23.85, -19.75) * mm});
            skLineSegment(sketch, "E94.9", {"start": v(12.1, 66) * mm, "end": v(12.1, 70.5) * mm});
            skLineSegment(sketch, "E94.10", {"start": v(12.1, 70.5) * mm, "end": v(-12.1, 70.5) * mm});
            skLineSegment(sketch, "E94.11", {"start": v(-12.1, 70.5) * mm, "end": v(-12.1, 66) * mm});
            skArc(sketch, "E94.12", {"start": v(-12.1, 66) * mm, "mid": v(-14.22, 60.87) * mm, "end": v(-19.35, 58.75) * mm});
            skLineSegment(sketch, "E94.13", {"start": v(-19.35, 58.75) * mm, "end": v(-23.85, 58.75) * mm});
            skArc(sketch, "E94.14", {"start": v(12.1, -27) * mm, "mid": v(14.22, -21.87) * mm, "end": v(19.35, -19.75) * mm});
            skLineSegment(sketch, "E94.15", {"start": v(-23.85, 58.75) * mm, "end": v(-23.85, -19.75) * mm});
            skSolve(sketch);
        }
        {
            var Q0;
            Q0 = qSketchRegion(id + "F15", true);
            var Q1;
            Q1 = qConstructionFilter(qBodyType(qCreatedBy(id + "F15" ,EDGE), BodyType.WIRE), ConstructionObject.NO);
            extrude(context, id + "F16", {"entities" : qUnion([Q0]), "surfaceEntities" : qUnion([Q1]), "depth" : 5 * mm, "offsetDistance" : 25 * mm});
        }
        {
            var Q0;
            Q0=makeQuery(id+"F1.opExtrude","CAP_FACE",FACE,{"disambiguationData":[OSD([sQuery(id+"F0.wireOp",EDGE,"E0.bottom"),sQuery(id+"F0.wireOp",EDGE,"E0.top"),sQuery(id+"F0.wireOp",EDGE,"E1"),sQuery(id+"F0.wireOp",EDGE,"E2"),sQuery(id+"F0.wireOp",EDGE,"E3.MirrorCS"),sQuery(id+"F0.wireOp",EDGE,"E4.MirrorCS"),sQuery(id+"F0.wireOp",EDGE,"E5.filletArc"),sQuery(id+"F0.wireOp",EDGE,"E6.filletArc"),sQuery(id+"F0.wireOp",EDGE,"E7.filletArc"),sQuery(id+"F0.wireOp",EDGE,"E8.filletArc"),sQuery(id+"F0.wireOp",EDGE,"E9.filletArc"),sQuery(id+"F0.wireOp",EDGE,"E10.filletArc"),sQuery(id+"F0.wireOp",EDGE,"E11.bottom"),sQuery(id+"F0.wireOp",EDGE,"E11.top"),sQuery(id+"F0.wireOp",EDGE,"E11.left"),sQuery(id+"F0.wireOp",EDGE,"E11.right"),sQuery(id+"F0.wireOp",EDGE,"E12.filletArc"),sQuery(id+"F0.wireOp",EDGE,"E13.filletArc"),sQuery(id+"F0.wireOp",EDGE,"E14.filletArc"),sQuery(id+"F0.wireOp",EDGE,"E15.filletArc")])],"isStart":false});
            var sketch = newSketch(context, id + "F17", { "sketchPlane" : qUnion([Q0])});
            skLineSegment(sketch, "E95.bottom", {"start": v(-20, 16) * mm, "end": v(20, 16) * mm});
            skLineSegment(sketch, "E95.top", {"start": v(-20, -57) * mm, "end": v(20, -57) * mm});
            skLineSegment(sketch, "E95.left", {"start": v(-20, 16) * mm, "end": v(-20, -57) * mm});
            skLineSegment(sketch, "E95.right", {"start": v(20, 16) * mm, "end": v(20, -57) * mm});
            skSolve(sketch);
        }
        {
            var Q0;
            Q0=makeQuery(id+"F17.imprint","IMPRINT",FACE,{"disambiguationData":[TD([[makeQuery(id+"F17.imprint","IMPRINT",EDGE,{"derivedFrom":sQuery(id+"F17.wireOp",EDGE,"E95.bottom")}),-1.0]])]});
            var Q1;
            Q1=makeQuery(id+"F17.imprint","IMPRINT",FACE,{"disambiguationData":[TD([[makeQuery(id+"F17.imprint","IMPRINT",EDGE,{"derivedFrom":makeQuery(id+"F1.opExtrude","CAP_EDGE",EDGE,{"disambiguationData":[OSD([sQuery(id+"F0.wireOp",EDGE,"E0.bottom")])],"isStart":false})}),1.0]])]});
            extrude(context, id + "F18", {"entities" : qUnion([Q0, Q1]), "depth" : 31 * mm, "offsetDistance" : 25 * mm});
        }
        {
            var Q0;
            Q0=makeQuery(id+"F14.boolean.opBoolean","COPY",FACE,{"derivedFrom":makeQuery(id+"F14.opExtrude","CAP_FACE",FACE,{"disambiguationData":[OSD([sQuery(id+"F13.wireOp",EDGE,"E70"),sQuery(id+"F13.wireOp",EDGE,"E71"),sQuery(id+"F13.wireOp",EDGE,"E72"),sQuery(id+"F13.wireOp",EDGE,"E73"),sQuery(id+"F13.wireOp",EDGE,"E76.MirrorCS"),sQuery(id+"F13.wireOp",EDGE,"E77.MirrorCS"),sQuery(id+"F13.wireOp",EDGE,"E78.MirrorCS"),sQuery(id+"F13.wireOp",EDGE,"E79.MirrorCS"),sQuery(id+"F13.wireOp",EDGE,"E80.MirrorCS"),sQuery(id+"F13.wireOp",EDGE,"E81.MirrorCS"),sQuery(id+"F13.wireOp",EDGE,"E82.MirrorCS"),sQuery(id+"F13.wireOp",EDGE,"E83.MirrorCS"),sQuery(id+"F13.wireOp",EDGE,"E84.MirrorCS"),sQuery(id+"F13.wireOp",EDGE,"E89"),sQuery(id+"F13.wireOp",EDGE,"E90"),sQuery(id+"F13.wireOp",EDGE,"E92")])],"isStart":false})});
            var sketch = newSketch(context, id + "F19", { "sketchPlane" : qUnion([Q0])});
            skLineSegment(sketch, "E96.bottom", {"start": v(-3.75, 64.5) * mm, "end": v(3.75, 64.5) * mm});
            skLineSegment(sketch, "E96.top", {"start": v(-3.75, 18.1) * mm, "end": v(3.75, 18.1) * mm});
            skLineSegment(sketch, "E96.left", {"start": v(-3.75, 64.5) * mm, "end": v(-3.75, 52.15) * mm});
            skLineSegment(sketch, "E96.right", {"start": v(3.75, 64.5) * mm, "end": v(3.75, 52.15) * mm});
            skLineSegment(sketch, "E97.bottom", {"start": v(8.1, 52.15) * mm, "end": v(3.75, 52.15) * mm});
            skLineSegment(sketch, "E97.top", {"start": v(8.1, 30.45) * mm, "end": v(3.75, 30.45) * mm});
            skLineSegment(sketch, "E97.left", {"start": v(8.1, 52.15) * mm, "end": v(8.1, 30.45) * mm});
            skLineSegment(sketch, "E97.right", {"start": v(-8.1, 52.15) * mm, "end": v(-8.1, 30.45) * mm});
            skPoint(sketch, "E97.middle", {"position": v(0, 41.3) * mm});
            skPoint(sketch, "E97.middle.positionSnap0", {"position": v(3.75, 41.3) * mm});
            skPoint(sketch, "E97.centerSnap0", {"position": v(3.75, 41.3) * mm});
            skLineSegment(sketch, "E98.trimOffspring", {"start": v(-3.75, 52.15) * mm, "end": v(-8.1, 52.15) * mm});
            skLineSegment(sketch, "E99.trimOffspring", {"start": v(-3.75, 30.45) * mm, "end": v(-3.75, 18.1) * mm});
            skLineSegment(sketch, "E100.trimOffspring", {"start": v(3.75, 30.45) * mm, "end": v(3.75, 18.1) * mm});
            skLineSegment(sketch, "E101.trimOffspring", {"start": v(-3.75, 30.45) * mm, "end": v(-8.1, 30.45) * mm});
            skSolve(sketch);
        }
        {
            var Q0;
            Q0=makeQuery(id+"F19.imprint","IMPRINT",FACE,{"disambiguationData":[TD([[makeQuery(id+"F19.imprint","IMPRINT",EDGE,{"derivedFrom":sQuery(id+"F19.wireOp",EDGE,"E96.bottom")}),-1.0]])]});
            extrude(context, id + "F20", {"entities" : qUnion([Q0]), "operationType" : NewBodyOperationType.REMOVE, "endBound" : BoundingType.THROUGH_ALL, "oppositeDirection" : true, "depth" : 25 * mm, "offsetDistance" : 25 * mm});
        }
        {
            var Q0;
            Q0=makeQuery(id+"F10.opExtrude","CAP_FACE",FACE,{"disambiguationData":[OSD([sQuery(id+"F9.wireOp",EDGE,"E54.0"),sQuery(id+"F9.wireOp",EDGE,"E55.0"),sQuery(id+"F9.wireOp",EDGE,"E56.0"),sQuery(id+"F9.wireOp",EDGE,"E57.0"),sQuery(id+"F9.wireOp",EDGE,"E58.0"),sQuery(id+"F9.wireOp",EDGE,"E59.0"),sQuery(id+"F9.wireOp",EDGE,"E60.0"),sQuery(id+"F9.wireOp",EDGE,"E61.0")])],"isStart":true});
            var sketch = newSketch(context, id + "F21", { "sketchPlane" : qUnion([Q0])});
            skCircle(sketch, "E102", {"center": v(0, 22) * mm, "radius": 9 * mm, "construction": true});
            skCircle(sketch, "E103", {"center": v(0, 22) * mm, "radius": 0.9 * mm});
            skCircle(sketch, "E104.1.0.0", {"center": v(2.7, 22) * mm, "radius": 0.9 * mm});
            skCircle(sketch, "E104.2.0.0", {"center": v(5.4, 22) * mm, "radius": 0.9 * mm});
            skCircle(sketch, "E104.3.0.0", {"center": v(8.1, 22) * mm, "radius": 0.9 * mm});
            skLineSegment(sketch, "E104.direction1", {"start": v(0, 22) * mm, "end": v(2.7, 22) * mm, "construction": true});
            skCircle(sketch, "E105.1.1", {"center": v(1.35, 24.34) * mm, "radius": 0.9 * mm});
            skCircle(sketch, "E105.1.2", {"center": v(2.7, 26.68) * mm, "radius": 0.9 * mm});
            skCircle(sketch, "E105.1.3", {"center": v(4.05, 29.01) * mm, "radius": 0.9 * mm});
            skCircle(sketch, "E105.2.1", {"center": v(-1.35, 24.34) * mm, "radius": 0.9 * mm});
            skCircle(sketch, "E105.2.2", {"center": v(-2.7, 26.68) * mm, "radius": 0.9 * mm});
            skCircle(sketch, "E105.2.3", {"center": v(-4.05, 29.01) * mm, "radius": 0.9 * mm});
            skCircle(sketch, "E105.3.1", {"center": v(-2.7, 22) * mm, "radius": 0.9 * mm});
            skCircle(sketch, "E105.3.2", {"center": v(-5.4, 22) * mm, "radius": 0.9 * mm});
            skCircle(sketch, "E105.3.3", {"center": v(-8.1, 22) * mm, "radius": 0.9 * mm});
            skCircle(sketch, "E105.4.1", {"center": v(-1.35, 19.66) * mm, "radius": 0.9 * mm});
            skCircle(sketch, "E105.4.2", {"center": v(-2.7, 17.32) * mm, "radius": 0.9 * mm});
            skCircle(sketch, "E105.4.3", {"center": v(-4.05, 14.99) * mm, "radius": 0.9 * mm});
            skCircle(sketch, "E105.5.1", {"center": v(1.35, 19.66) * mm, "radius": 0.9 * mm});
            skCircle(sketch, "E105.5.2", {"center": v(2.7, 17.32) * mm, "radius": 0.9 * mm});
            skCircle(sketch, "E105.5.3", {"center": v(4.05, 14.99) * mm, "radius": 0.9 * mm});
            skCircle(sketch, "E106", {"center": v(0, 22) * mm, "radius": 2.7 * mm, "construction": true});
            skCircle(sketch, "E107", {"center": v(0, 22) * mm, "radius": 5.4 * mm, "construction": true});
            skCircle(sketch, "E108", {"center": v(0, 22) * mm, "radius": 8.1 * mm, "construction": true});
            skCircle(sketch, "E109", {"center": v(0, 22) * mm, "radius": 4.35 * mm, "construction": true});
            skLineSegment(sketch, "E110", {"start": v(0, 24.7) * mm, "end": v(0, 27.4) * mm, "construction": true});
            skPoint(sketch, "E111", {"position": v(0, 26.35) * mm});
            skLineSegment(sketch, "E112", {"start": v(0, 27.4) * mm, "end": v(0, 30.1) * mm, "construction": true});
            skPoint(sketch, "E113", {"position": v(0, 28.75) * mm});
            skCircle(sketch, "E114", {"center": v(-3.77, 24.18) * mm, "radius": 0.9 * mm});
            skLineSegment(sketch, "E115", {"start": v(-3.77, 24.18) * mm, "end": v(0, 22) * mm, "construction": true});
            skCircle(sketch, "E116.1.0", {"center": v(-3.77, 19.83) * mm, "radius": 0.9 * mm});
            skCircle(sketch, "E116.2.0", {"center": v(0, 17.65) * mm, "radius": 0.9 * mm});
            skCircle(sketch, "E116.3.0", {"center": v(3.77, 19.83) * mm, "radius": 0.9 * mm});
            skCircle(sketch, "E116.4.0", {"center": v(3.77, 24.18) * mm, "radius": 0.9 * mm});
            skCircle(sketch, "E116.5.0", {"center": v(0, 26.35) * mm, "radius": 0.9 * mm});
            skCircle(sketch, "E117", {"center": v(0, 22) * mm, "radius": 6.75 * mm, "construction": true});
            skCircle(sketch, "E118", {"center": v(-6.34, 24.3) * mm, "radius": 0.9 * mm});
            skCircle(sketch, "E119", {"center": v(-5.17, 26.34) * mm, "radius": 0.9 * mm});
            skLineSegment(sketch, "E120", {"start": v(-5.17, 26.34) * mm, "end": v(0, 22) * mm, "construction": true});
            skLineSegment(sketch, "E121", {"start": v(-6.34, 24.3) * mm, "end": v(0, 22) * mm, "construction": true});
            skCircle(sketch, "E122.1.0", {"center": v(-6.34, 19.7) * mm, "radius": 0.9 * mm});
            skCircle(sketch, "E122.1.1", {"center": v(-5.17, 17.66) * mm, "radius": 0.9 * mm});
            skCircle(sketch, "E122.2.0", {"center": v(-1.17, 15.35) * mm, "radius": 0.9 * mm});
            skCircle(sketch, "E122.2.1", {"center": v(1.17, 15.35) * mm, "radius": 0.9 * mm});
            skCircle(sketch, "E122.3.0", {"center": v(5.17, 17.66) * mm, "radius": 0.9 * mm});
            skCircle(sketch, "E122.3.1", {"center": v(6.34, 19.7) * mm, "radius": 0.9 * mm});
            skCircle(sketch, "E122.4.0", {"center": v(6.34, 24.3) * mm, "radius": 0.9 * mm});
            skCircle(sketch, "E122.4.1", {"center": v(5.17, 26.34) * mm, "radius": 0.9 * mm});
            skCircle(sketch, "E122.5.0", {"center": v(1.17, 28.65) * mm, "radius": 0.9 * mm});
            skCircle(sketch, "E122.5.1", {"center": v(-1.17, 28.65) * mm, "radius": 0.9 * mm});
            skCircle(sketch, "E123", {"center": v(0, 22) * mm, "radius": 8.7 * mm, "construction": true});
            skCircle(sketch, "E124", {"center": v(0, 30.7) * mm, "radius": 0.9 * mm});
            skCircle(sketch, "E125.1.0", {"center": v(-7.53, 26.35) * mm, "radius": 0.9 * mm});
            skCircle(sketch, "E125.2.0", {"center": v(-7.53, 17.65) * mm, "radius": 0.9 * mm});
            skCircle(sketch, "E125.3.0", {"center": v(0, 13.3) * mm, "radius": 0.9 * mm});
            skCircle(sketch, "E125.4.0", {"center": v(7.53, 17.65) * mm, "radius": 0.9 * mm});
            skCircle(sketch, "E125.5.0", {"center": v(7.53, 26.35) * mm, "radius": 0.9 * mm});
            skSolve(sketch);
        }
        {
            var Q0;
            Q0 = qSketchRegion(id + "F21", true);
            extrude(context, id + "F22", {"entities" : qUnion([Q0]), "operationType" : NewBodyOperationType.REMOVE, "endBound" : BoundingType.THROUGH_ALL, "oppositeDirection" : true, "depth" : 25 * mm, "offsetDistance" : 25 * mm});
        }
        {
            var Q0;
            Q0=makeQuery(id+"F16.opExtrude","CAP_FACE",FACE,{"disambiguationData":[OSD([sQuery(id+"F15.wireOp",EDGE,"E93.0"),sQuery(id+"F15.wireOp",EDGE,"E93.1"),sQuery(id+"F15.wireOp",EDGE,"E93.2"),sQuery(id+"F15.wireOp",EDGE,"E93.3"),sQuery(id+"F15.wireOp",EDGE,"E93.4"),sQuery(id+"F15.wireOp",EDGE,"E93.5"),sQuery(id+"F15.wireOp",EDGE,"E93.6"),sQuery(id+"F15.wireOp",EDGE,"E93.7"),sQuery(id+"F15.wireOp",EDGE,"E93.8"),sQuery(id+"F15.wireOp",EDGE,"E93.9"),sQuery(id+"F15.wireOp",EDGE,"E93.10"),sQuery(id+"F15.wireOp",EDGE,"E93.11"),sQuery(id+"F15.wireOp",EDGE,"E93.12"),sQuery(id+"F15.wireOp",EDGE,"E93.13"),sQuery(id+"F15.wireOp",EDGE,"E93.14"),sQuery(id+"F15.wireOp",EDGE,"E93.15"),sQuery(id+"F15.wireOp",EDGE,"E94.0"),sQuery(id+"F15.wireOp",EDGE,"E94.1"),sQuery(id+"F15.wireOp",EDGE,"E94.2"),sQuery(id+"F15.wireOp",EDGE,"E94.3"),sQuery(id+"F15.wireOp",EDGE,"E94.4"),sQuery(id+"F15.wireOp",EDGE,"E94.5"),sQuery(id+"F15.wireOp",EDGE,"E94.6"),sQuery(id+"F15.wireOp",EDGE,"E94.7"),sQuery(id+"F15.wireOp",EDGE,"E94.8"),sQuery(id+"F15.wireOp",EDGE,"E94.9"),sQuery(id+"F15.wireOp",EDGE,"E94.10"),sQuery(id+"F15.wireOp",EDGE,"E94.11"),sQuery(id+"F15.wireOp",EDGE,"E94.12"),sQuery(id+"F15.wireOp",EDGE,"E94.13"),sQuery(id+"F15.wireOp",EDGE,"E94.14"),sQuery(id+"F15.wireOp",EDGE,"E94.15")])],"isStart":false});
            var sketch = newSketch(context, id + "F23", { "sketchPlane" : qUnion([Q0])});
            skLineSegment(sketch, "E126.bottom", {"start": v(25.75, 15.95) * mm, "end": v(-25.75, 15.95) * mm});
            skLineSegment(sketch, "E126.top", {"start": v(25.75, -20.05) * mm, "end": v(-25.75, -20.05) * mm});
            skLineSegment(sketch, "E126.left", {"start": v(25.75, 15.95) * mm, "end": v(25.75, -20.05) * mm});
            skLineSegment(sketch, "E126.right", {"start": v(-25.75, 15.95) * mm, "end": v(-25.75, -20.05) * mm});
            skPoint(sketch, "E126.middle", {"position": v(0, -2.05) * mm});
            skSolve(sketch);
        }
        {
            var Q0;
            Q0 = qSketchRegion(id + "F23", true);
            extrude(context, id + "F24", {"entities" : qUnion([Q0]), "operationType" : NewBodyOperationType.REMOVE, "oppositeDirection" : true, "depth" : 1.5 * mm, "offsetDistance" : 25 * mm});
        }
        {
            var Q0;
            Q0=makeQuery(id+"F5.boolean.opBoolean","COPY",FACE,{"derivedFrom":makeQuery(id+"F5.opExtrude","CAP_FACE",FACE,{"disambiguationData":[OSD([sQuery(id+"F4.wireOp",EDGE,"E37.0"),sQuery(id+"F4.wireOp",EDGE,"E38.0")])],"isStart":false})});
            var sketch = newSketch(context, id + "F25", { "sketchPlane" : qUnion([Q0])});
            skCircle(sketch, "E127.0", {"center": v(-19.35, 66) * mm, "radius": 2.25 * mm});
            skCircle(sketch, "E128.0", {"center": v(19.35, 66) * mm, "radius": 2.25 * mm});
            skCircle(sketch, "E129.0", {"center": v(19.35, -27) * mm, "radius": 2.25 * mm});
            skCircle(sketch, "E130.0", {"center": v(-19.35, -27) * mm, "radius": 2.25 * mm});
            skSolve(sketch);
        }
        {
            var Q0;
            Q0 = qSketchRegion(id + "F25", true);
            extrude(context, id + "F26", {"entities" : qUnion([Q0]), "operationType" : NewBodyOperationType.REMOVE, "endBound" : BoundingType.THROUGH_ALL, "oppositeDirection" : true, "depth" : 25 * mm, "offsetDistance" : 25 * mm});
        }
        {
            var Q0;
            Q0=makeQuery(id+"F18.opExtrude","CAP_FACE",FACE,{"disambiguationData":[OSD([sQuery(id+"F17.wireOp",EDGE,"E95.bottom"),sQuery(id+"F17.wireOp",EDGE,"E95.top"),sQuery(id+"F17.wireOp",EDGE,"E95.left"),sQuery(id+"F17.wireOp",EDGE,"E95.right")])],"isStart":true});
            var sketch = newSketch(context, id + "F27", { "sketchPlane" : qUnion([Q0])});
            skArc(sketch, "E131.0", {"start": v(-17.19, -0.7) * mm, "mid": v(-17.48, 0) * mm, "end": v(-17.19, 0.7) * mm});
            skLineSegment(sketch, "E131.1", {"start": v(17.19, 0.7) * mm, "end": v(12.41, 5.48) * mm});
            skArc(sketch, "E131.2", {"start": v(9.23, 6.8) * mm, "mid": v(10.95, 6.46) * mm, "end": v(12.41, 5.48) * mm});
            skLineSegment(sketch, "E131.3", {"start": v(9.23, 6.8) * mm, "end": v(-9.23, 6.8) * mm});
            skArc(sketch, "E131.4", {"start": v(-12.41, 5.48) * mm, "mid": v(-10.95, 6.46) * mm, "end": v(-9.23, 6.8) * mm});
            skArc(sketch, "E131.5", {"start": v(17.19, 0.7) * mm, "mid": v(17.48, 0) * mm, "end": v(17.19, -0.7) * mm});
            skLineSegment(sketch, "E131.6", {"start": v(-17.19, 0.7) * mm, "end": v(-12.41, 5.48) * mm});
            skLineSegment(sketch, "E131.7", {"start": v(12.41, -5.48) * mm, "end": v(17.19, -0.7) * mm});
            skArc(sketch, "E131.8", {"start": v(12.41, -5.48) * mm, "mid": v(10.95, -6.46) * mm, "end": v(9.23, -6.8) * mm});
            skLineSegment(sketch, "E131.9", {"start": v(9.23, -6.8) * mm, "end": v(-9.23, -6.8) * mm});
            skArc(sketch, "E131.10", {"start": v(-9.23, -6.8) * mm, "mid": v(-10.95, -6.46) * mm, "end": v(-12.41, -5.48) * mm});
            skLineSegment(sketch, "E131.11", {"start": v(-12.41, -5.48) * mm, "end": v(-17.19, -0.7) * mm});
            skSolve(sketch);
        }
        {
            var Q0;
            Q0 = qSketchRegion(id + "F27", true);
            extrude(context, id + "F28", {"entities" : qUnion([Q0]), "operationType" : NewBodyOperationType.ADD, "depth" : 19 * mm, "offsetDistance" : 25 * mm});
        }
        {
            var Q0;
            Q0=makeQuery(id+"F14.boolean.opBoolean","COPY",FACE,{"derivedFrom":makeQuery(id+"F14.opExtrude","CAP_FACE",FACE,{"disambiguationData":[OSD([sQuery(id+"F13.wireOp",EDGE,"E70"),sQuery(id+"F13.wireOp",EDGE,"E71"),sQuery(id+"F13.wireOp",EDGE,"E72"),sQuery(id+"F13.wireOp",EDGE,"E73"),sQuery(id+"F13.wireOp",EDGE,"E76.MirrorCS"),sQuery(id+"F13.wireOp",EDGE,"E77.MirrorCS"),sQuery(id+"F13.wireOp",EDGE,"E78.MirrorCS"),sQuery(id+"F13.wireOp",EDGE,"E79.MirrorCS"),sQuery(id+"F13.wireOp",EDGE,"E80.MirrorCS"),sQuery(id+"F13.wireOp",EDGE,"E81.MirrorCS"),sQuery(id+"F13.wireOp",EDGE,"E82.MirrorCS"),sQuery(id+"F13.wireOp",EDGE,"E83.MirrorCS"),sQuery(id+"F13.wireOp",EDGE,"E84.MirrorCS"),sQuery(id+"F13.wireOp",EDGE,"E89"),sQuery(id+"F13.wireOp",EDGE,"E90"),sQuery(id+"F13.wireOp",EDGE,"E92")])],"isStart":false})});
            var sketch = newSketch(context, id + "F29", { "sketchPlane" : qUnion([Q0])});
            skLineSegment(sketch, "E132", {"start": v(-8.1, 30.45) * mm, "end": v(8.1, 52.15) * mm, "construction": true});
            skLineSegment(sketch, "E133.bottom", {"start": v(-12.5, 68.8) * mm, "end": v(12.5, 68.8) * mm});
            skLineSegment(sketch, "E133.top", {"start": v(-12.5, 13.8) * mm, "end": v(12.5, 13.8) * mm});
            skLineSegment(sketch, "E133.left", {"start": v(-12.5, 68.8) * mm, "end": v(-12.5, 13.8) * mm});
            skLineSegment(sketch, "E133.right", {"start": v(12.5, 68.8) * mm, "end": v(12.5, 13.8) * mm});
            skPoint(sketch, "E133.middle", {"position": v(0, 41.3) * mm});
            skSolve(sketch);
        }
        {
            var Q0;
            Q0 = qSketchRegion(id + "F29", true);
            extrude(context, id + "F30", {"entities" : qUnion([Q0]), "operationType" : NewBodyOperationType.REMOVE, "oppositeDirection" : true, "depth" : 1 * mm, "offsetDistance" : 25 * mm});
        }
        {
            var Q0;
            Q0=makeQuery(id+"F10.opExtrude","SWEPT_FACE",FACE,{"disambiguationData":[OSD([sQuery(id+"F9.wireOp",EDGE,"E58.0")])]});
            var Q1;
            Q1=makeQuery(id+"F10.opExtrude","SWEPT_FACE",FACE,{"disambiguationData":[OSD([sQuery(id+"F9.wireOp",EDGE,"E54.0")])]});
            cPlane(context, id + "F31", {"entities" : qUnion([Q0, Q1]), "cplaneType" : CPlaneType.MID_PLANE, "offset" : 25 * mm, "width" : 150 * mm, "height" : 150 * mm});
        }
        {
            var Q0;
            Q0=makeQuery(id+"F14.boolean.opBoolean","COPY",FACE,{"derivedFrom":makeQuery(id+"F14.opExtrude","SWEPT_FACE",FACE,{"disambiguationData":[OSD([sQuery(id+"F13.wireOp",EDGE,"E71")])]})});
            var sketch = newSketch(context, id + "F32", { "sketchPlane" : qUnion([Q0])});
            skLineSegment(sketch, "E134.0", {"start": v(-60.75, 49.5) * mm, "end": v(-60.75, 16.5) * mm, "construction": true});
            skLineSegment(sketch, "E135.0", {"start": v(-60.75, 49.5) * mm, "end": v(-66, 49.5) * mm});
            skLineSegment(sketch, "E136.0", {"start": v(-66, 49.5) * mm, "end": v(-72.5, 49.5) * mm});
            skLineSegment(sketch, "E137", {"start": v(-60.75, 22.75) * mm, "end": v(-72.5, 34.5) * mm});
            skLineSegment(sketch, "E138", {"start": v(-72.5, 34.5) * mm, "end": v(-72.5, 49.5) * mm});
            skLineSegment(sketch, "E139", {"start": v(-60.75, 49.5) * mm, "end": v(-60.75, 22.75) * mm});
            skSolve(sketch);
        }
        {
            var Q0;
            Q0 = qSketchRegion(id + "F32", true);
            var Q1;
            Q1=sQuery(id+"F32.wireOp",EDGE,"E139");
            revolve(context, id + "F33", {"operationType" : NewBodyOperationType.REMOVE, "entities" : qUnion([Q0]), "axis" : qUnion([Q1]), "revolveType" : RevolveType.FULL, "oppositeDirection" : true});
        }
    });
